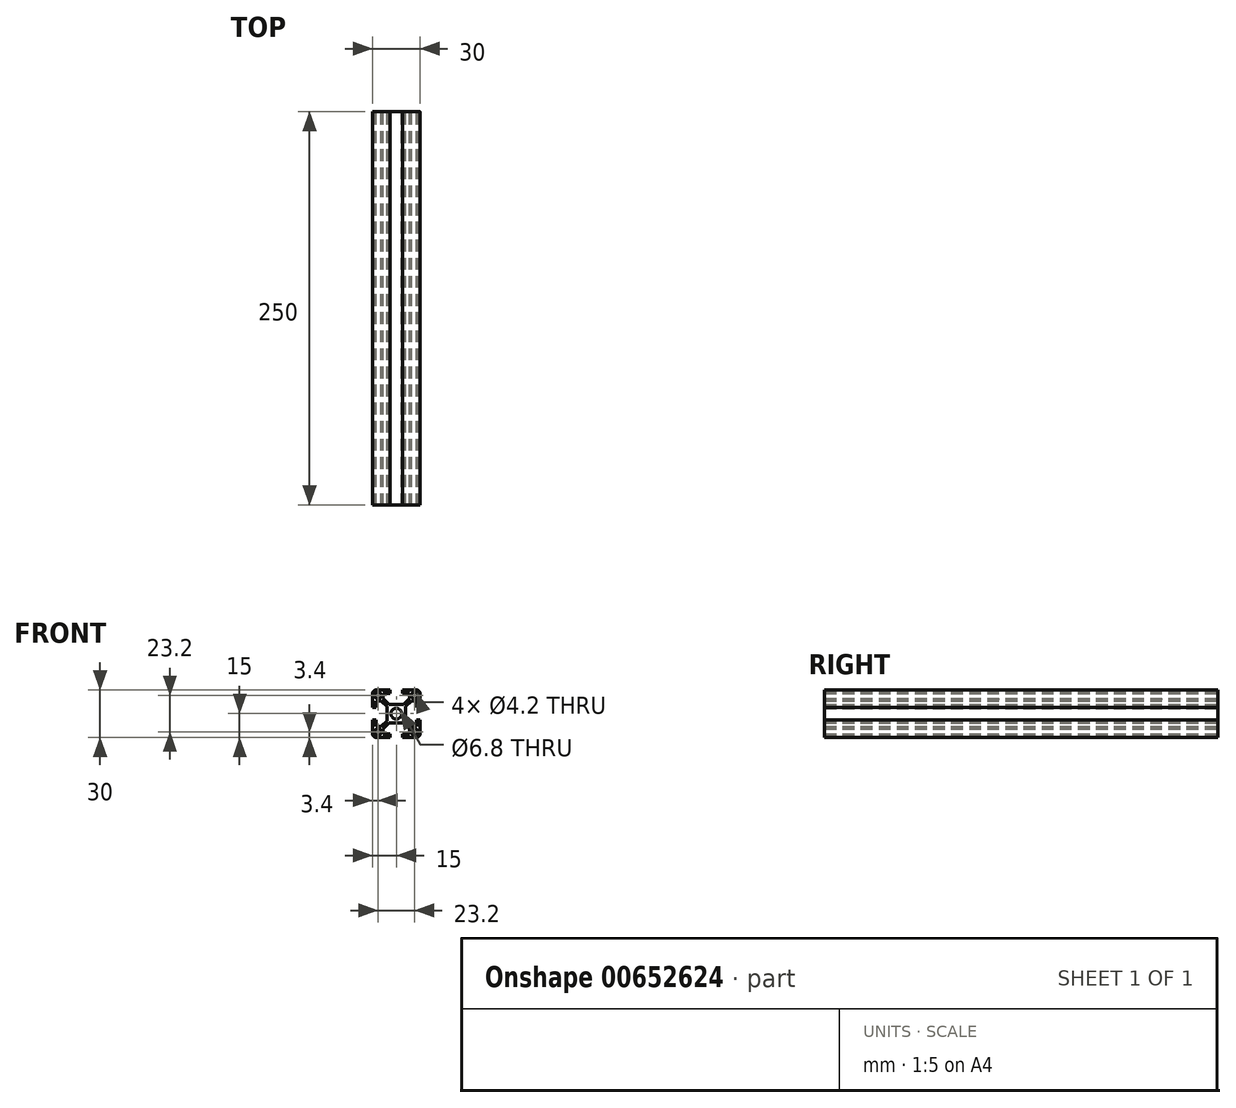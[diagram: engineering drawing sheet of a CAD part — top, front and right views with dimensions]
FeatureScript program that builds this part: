
annotation { "Feature Type Name" : "Feature", "Feature Type Description" : "" }
export const myFeature = defineFeature(function(context is Context, id is Id, definition is map)
    precondition{}
    {
        {
            var Q0;
            Q0=qCreatedBy(makeId("Front.planeOp"),FACE);
            var sketch = newSketch(context, id + "F0", { "sketchPlane" : qUnion([Q0])});
            skLineSegment(sketch, "E0", {"start": v(0, 6) * mm, "end": v(-4.59, 6) * mm});
            skLineSegment(sketch, "E1", {"start": v(-4.59, 6) * mm, "end": v(-8.25, 9.66) * mm});
            skLineSegment(sketch, "E2", {"start": v(-8.25, 9.66) * mm, "end": v(-8.25, 13) * mm});
            skLineSegment(sketch, "E3", {"start": v(-8.25, 13) * mm, "end": v(-4, 13) * mm});
            skLineSegment(sketch, "E4", {"start": v(-4, 13) * mm, "end": v(-4, 15) * mm});
            skLineSegment(sketch, "E5", {"start": v(-4, 15) * mm, "end": v(-13, 15) * mm});
            skLineSegment(sketch, "E6", {"start": v(-15, 13) * mm, "end": v(-15, 4) * mm});
            skLineSegment(sketch, "E7", {"start": v(-15, 4) * mm, "end": v(-13, 4) * mm});
            skLineSegment(sketch, "E8", {"start": v(-13, 4) * mm, "end": v(-13, 8.25) * mm});
            skLineSegment(sketch, "E9", {"start": v(-13, 8.25) * mm, "end": v(-9.66, 8.25) * mm});
            skLineSegment(sketch, "E10", {"start": v(-9.66, 8.25) * mm, "end": v(-6, 4.59) * mm});
            skLineSegment(sketch, "E11", {"start": v(-6, 4.59) * mm, "end": v(-6, 0) * mm});
            skLineSegment(sketch, "E12", {"start": v(-6, 0) * mm, "end": v(0, 0) * mm, "construction": true});
            skLineSegment(sketch, "E13", {"start": v(0, 0) * mm, "end": v(0, 6) * mm, "construction": true});
            skArc(sketch, "E14", {"start": v(0, 3.4) * mm, "mid": v(-2.4, 2.4) * mm, "end": v(-3.4, 0) * mm});
            skCircle(sketch, "E15", {"center": v(-11.6, 11.6) * mm, "radius": 2.1 * mm});
            skLineSegment(sketch, "E16", {"start": v(0, 0) * mm, "end": v(-7.38, 7.38) * mm, "construction": true});
            skLineSegment(sketch, "E17.1.0", {"start": v(-8.25, -13) * mm, "end": v(-8.25, -9.66) * mm});
            skLineSegment(sketch, "E17.1.1", {"start": v(-4, -15) * mm, "end": v(-4, -13) * mm});
            skLineSegment(sketch, "E17.1.2", {"start": v(-4, -13) * mm, "end": v(-8.25, -13) * mm});
            skLineSegment(sketch, "E17.1.3", {"start": v(-15, -4) * mm, "end": v(-15, -13) * mm});
            skLineSegment(sketch, "E17.1.4", {"start": v(-8.25, -9.66) * mm, "end": v(-4.59, -6) * mm});
            skLineSegment(sketch, "E17.1.5", {"start": v(-13, -15) * mm, "end": v(-4, -15) * mm});
            skLineSegment(sketch, "E17.1.6", {"start": v(-4.59, -6) * mm, "end": v(0, -6) * mm});
            skLineSegment(sketch, "E17.1.7", {"start": v(0, -6) * mm, "end": v(0, 0) * mm, "construction": true});
            skLineSegment(sketch, "E17.1.8", {"start": v(0, 0) * mm, "end": v(-6, 0) * mm, "construction": true});
            skLineSegment(sketch, "E17.1.9", {"start": v(-13, -4) * mm, "end": v(-15, -4) * mm});
            skLineSegment(sketch, "E17.1.10", {"start": v(-13, -8.25) * mm, "end": v(-13, -4) * mm});
            skArc(sketch, "E17.1.11", {"start": v(-3.4, 0) * mm, "mid": v(-2.4, -2.4) * mm, "end": v(0, -3.4) * mm});
            skLineSegment(sketch, "E17.1.12", {"start": v(-9.66, -8.25) * mm, "end": v(-13, -8.25) * mm});
            skLineSegment(sketch, "E17.1.13", {"start": v(0, 0) * mm, "end": v(-7.38, -7.38) * mm, "construction": true});
            skLineSegment(sketch, "E17.1.14", {"start": v(-6, -4.59) * mm, "end": v(-9.66, -8.25) * mm});
            skCircle(sketch, "E17.1.15", {"center": v(-11.6, -11.6) * mm, "radius": 2.1 * mm});
            skLineSegment(sketch, "E17.1.16", {"start": v(-6, 0) * mm, "end": v(-6, -4.59) * mm});
            skLineSegment(sketch, "E17.2.0", {"start": v(13, -8.25) * mm, "end": v(9.66, -8.25) * mm});
            skLineSegment(sketch, "E17.2.1", {"start": v(15, -4) * mm, "end": v(13, -4) * mm});
            skLineSegment(sketch, "E17.2.2", {"start": v(13, -4) * mm, "end": v(13, -8.25) * mm});
            skLineSegment(sketch, "E17.2.3", {"start": v(4, -15) * mm, "end": v(13, -15) * mm});
            skLineSegment(sketch, "E17.2.4", {"start": v(9.66, -8.25) * mm, "end": v(6, -4.59) * mm});
            skLineSegment(sketch, "E17.2.5", {"start": v(15, -13) * mm, "end": v(15, -4) * mm});
            skLineSegment(sketch, "E17.2.6", {"start": v(6, -4.59) * mm, "end": v(6, 0) * mm});
            skLineSegment(sketch, "E17.2.7", {"start": v(6, 0) * mm, "end": v(0, 0) * mm, "construction": true});
            skLineSegment(sketch, "E17.2.8", {"start": v(0, 0) * mm, "end": v(0, -6) * mm, "construction": true});
            skLineSegment(sketch, "E17.2.9", {"start": v(4, -13) * mm, "end": v(4, -15) * mm});
            skLineSegment(sketch, "E17.2.10", {"start": v(8.25, -13) * mm, "end": v(4, -13) * mm});
            skArc(sketch, "E17.2.11", {"start": v(0, -3.4) * mm, "mid": v(2.4, -2.4) * mm, "end": v(3.4, 0) * mm});
            skLineSegment(sketch, "E17.2.12", {"start": v(8.25, -9.66) * mm, "end": v(8.25, -13) * mm});
            skLineSegment(sketch, "E17.2.13", {"start": v(0, 0) * mm, "end": v(7.38, -7.38) * mm, "construction": true});
            skLineSegment(sketch, "E17.2.14", {"start": v(4.59, -6) * mm, "end": v(8.25, -9.66) * mm});
            skCircle(sketch, "E17.2.15", {"center": v(11.6, -11.6) * mm, "radius": 2.1 * mm});
            skLineSegment(sketch, "E17.2.16", {"start": v(0, -6) * mm, "end": v(4.59, -6) * mm});
            skLineSegment(sketch, "E17.3.0", {"start": v(8.25, 13) * mm, "end": v(8.25, 9.66) * mm});
            skLineSegment(sketch, "E17.3.1", {"start": v(4, 15) * mm, "end": v(4, 13) * mm});
            skLineSegment(sketch, "E17.3.2", {"start": v(4, 13) * mm, "end": v(8.25, 13) * mm});
            skLineSegment(sketch, "E17.3.3", {"start": v(15, 4) * mm, "end": v(15, 13) * mm});
            skLineSegment(sketch, "E17.3.4", {"start": v(8.25, 9.66) * mm, "end": v(4.59, 6) * mm});
            skLineSegment(sketch, "E17.3.5", {"start": v(13, 15) * mm, "end": v(4, 15) * mm});
            skLineSegment(sketch, "E17.3.6", {"start": v(4.59, 6) * mm, "end": v(0, 6) * mm});
            skLineSegment(sketch, "E17.3.7", {"start": v(0, 6) * mm, "end": v(0, 0) * mm, "construction": true});
            skLineSegment(sketch, "E17.3.8", {"start": v(0, 0) * mm, "end": v(6, 0) * mm, "construction": true});
            skLineSegment(sketch, "E17.3.9", {"start": v(13, 4) * mm, "end": v(15, 4) * mm});
            skLineSegment(sketch, "E17.3.10", {"start": v(13, 8.25) * mm, "end": v(13, 4) * mm});
            skArc(sketch, "E17.3.11", {"start": v(3.4, 0) * mm, "mid": v(2.4, 2.4) * mm, "end": v(0, 3.4) * mm});
            skLineSegment(sketch, "E17.3.12", {"start": v(9.66, 8.25) * mm, "end": v(13, 8.25) * mm});
            skLineSegment(sketch, "E17.3.13", {"start": v(0, 0) * mm, "end": v(7.38, 7.38) * mm, "construction": true});
            skLineSegment(sketch, "E17.3.14", {"start": v(6, 4.59) * mm, "end": v(9.66, 8.25) * mm});
            skCircle(sketch, "E17.3.15", {"center": v(11.6, 11.6) * mm, "radius": 2.1 * mm});
            skLineSegment(sketch, "E17.3.16", {"start": v(6, 0) * mm, "end": v(6, 4.59) * mm});
            skPoint(sketch, "E18.visualSharp", {"position": v(-15, 15) * mm});
            skArc(sketch, "E18.filletArc", {"start": v(-13, 15) * mm, "mid": v(-14.41, 14.41) * mm, "end": v(-15, 13) * mm});
            skPoint(sketch, "E19.visualSharp", {"position": v(15, 15) * mm});
            skArc(sketch, "E19.filletArc", {"start": v(15, 13) * mm, "mid": v(14.41, 14.41) * mm, "end": v(13, 15) * mm});
            skPoint(sketch, "E20.visualSharp", {"position": v(15, -15) * mm});
            skArc(sketch, "E20.filletArc", {"start": v(13, -15) * mm, "mid": v(14.41, -14.41) * mm, "end": v(15, -13) * mm});
            skPoint(sketch, "E21.visualSharp", {"position": v(-15, -15) * mm});
            skArc(sketch, "E21.filletArc", {"start": v(-15, -13) * mm, "mid": v(-14.41, -14.41) * mm, "end": v(-13, -15) * mm});
            skSolve(sketch);
        }
        {
            var Q0;
            Q0 = qSketchRegion(id + "F0", true);
            extrude(context, id + "F1", {"entities" : qUnion([Q0]), "depth" : 250 * mm, "offsetDistance" : 25 * mm});
        }
    });
